# Revit family: RS_58x.60
name_source: partatom
category: Sanitärinstallationen
units: mm (PartAtom-declared; Revit-internal decimal feet)

## family parameters
Arbeitsebenenbasiert = Nein
Beim Laden mit Abzugskörper schneiden = Nein
Bemaßung runder Anschluss = Durchmesser verwenden
Gemeinsam genutzt = Nein
Immer vertikal = Ja
Raumberechnungspunkt = Nein
Teiletyp = Normal

## types (2) — shared parameters
Abwasserrohrverbindung = Nein
Baugruppenkennzeichen = D2030300
HW-Verbindung = Nein
KW-Verbindung = Ja
Lüftungsverbindung = Nein
Modell = 100x100
RS_D110 = 64 mm  [stored 0.209974 ft]
RS_D1d = 64 mm  [stored 0.209974 ft]
RS_Manufacture = Resitec
RS_Sd = 115 mm  [stored 0.377297 ft]
RS_diasenk = 76 mm
RS_dim001 = 5 mm  [stored 0.0164042 ft]
RS_dim003 = 152 mm
RS_dim009 = 35 mm  [stored 0.114829 ft]
RS_dimDeck = 130 mm  [stored 0.426509 ft]
RS_dimRgL = 200 mm  [stored 0.656168 ft]
RS_dimpfad01 = 315 mm
RS_s1 = 3 mm  [stored 0.00984252 ft]
RS_s2 = 2 mm  [stored 0.00656168 ft]
URL = https://www.resitec.ch
V max = 230
zero-valued in all types: Vorgabe-Ansicht

## per-type parameters (varying)
| type | RS_dimRg |
| DN80 | 350 mm  [stored 1.14829 ft] |
| DN100 | 300 mm |

note: [stored X ft] marks values corroborated as IEEE doubles in the binary element streams (Revit-internal decimal feet)
